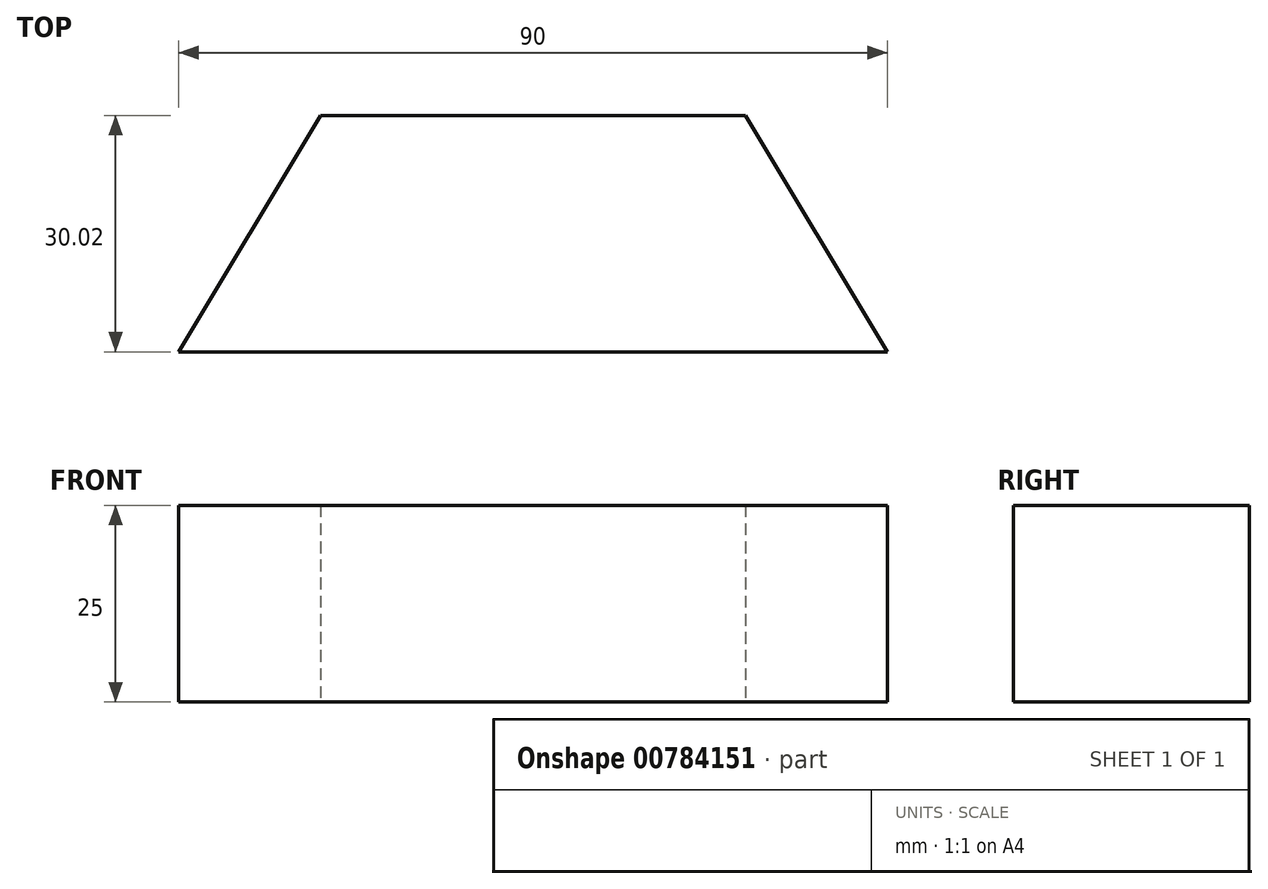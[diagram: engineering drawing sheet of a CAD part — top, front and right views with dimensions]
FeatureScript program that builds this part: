
annotation { "Feature Type Name" : "Feature", "Feature Type Description" : "" }
export const myFeature = defineFeature(function(context is Context, id is Id, definition is map)
    precondition{}
    {
        {
            var Q0;
            Q0=qCreatedBy(makeId("Top.planeOp"),FACE);
            var sketch = newSketch(context, id + "F0", { "sketchPlane" : qUnion([Q0])});
            skLineSegment(sketch, "E0.bottom", {"start": v(45, 0) * mm, "end": v(-45, 0) * mm});
            skLineSegment(sketch, "E0.top", {"start": v(27, 30.02) * mm, "end": v(-27, 30.02) * mm});
            skPoint(sketch, "E0.middle", {"position": v(0, 0) * mm});
            skLineSegment(sketch, "E1", {"start": v(-45, 0) * mm, "end": v(-27, 30.02) * mm});
            skLineSegment(sketch, "E2", {"start": v(27, 30.02) * mm, "end": v(45, 0) * mm});
            skSolve(sketch);
        }
        {
            var Q0;
            Q0=makeQuery(id+"F0.imprint","IMPRINT",FACE,{"disambiguationData":[TD([[makeQuery(id+"F0.imprint","IMPRINT",EDGE,{"derivedFrom":sQuery(id+"F0.wireOp",EDGE,"E0.bottom")}),-1.0]])]});
            extrude(context, id + "F1", {"entities" : qUnion([Q0]), "depth" : 25 * mm, "offsetDistance" : 25 * mm});
        }
    });
